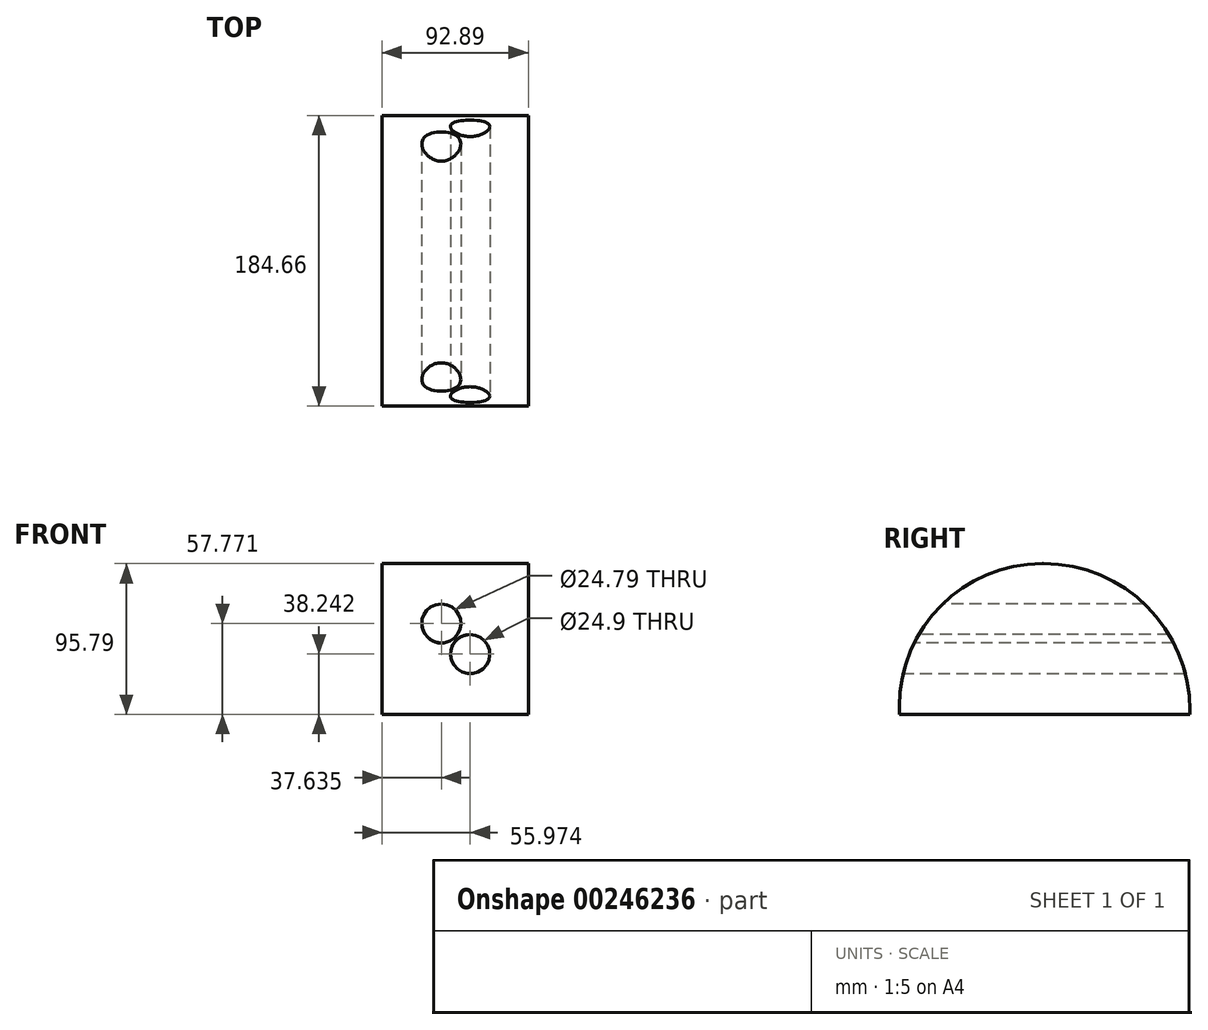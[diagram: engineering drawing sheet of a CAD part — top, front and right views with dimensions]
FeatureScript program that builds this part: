
annotation { "Feature Type Name" : "Feature", "Feature Type Description" : "" }
export const myFeature = defineFeature(function(context is Context, id is Id, definition is map)
    precondition{}
    {
        {
            var Q0;
            Q0=qCreatedBy(makeId("Front.planeOp"),FACE);
            var sketch = newSketch(context, id + "F0", { "sketchPlane" : qUnion([Q0])});
            skLineSegment(sketch, "E0.bottom", {"start": v(-52.5, 35.25) * mm, "end": v(40.39, 35.25) * mm});
            skLineSegment(sketch, "E0.top", {"start": v(-52.5, -60.54) * mm, "end": v(40.39, -60.54) * mm});
            skLineSegment(sketch, "E0.left", {"start": v(-52.5, 35.25) * mm, "end": v(-52.5, -60.54) * mm});
            skLineSegment(sketch, "E0.right", {"start": v(40.39, 35.25) * mm, "end": v(40.39, -60.54) * mm});
            skSolve(sketch);
        }
        {
            var Q0;
            Q0=makeQuery(id+"F0.imprint","IMPRINT",FACE,{"disambiguationData":[TD([[makeQuery(id+"F0.imprint","IMPRINT",EDGE,{"derivedFrom":sQuery(id+"F0.wireOp",EDGE,"E0.bottom")}),-1.0]])]});
            extrude(context, id + "F1", {"entities" : qUnion([Q0]), "depth" : 98.55 * mm});
        }
        {
            var Q0;
            Q0=makeQuery(id+"F1.opExtrude","CAP_FACE",FACE,{"disambiguationData":[OSD([sQuery(id+"F0.wireOp",EDGE,"E0.bottom"),sQuery(id+"F0.wireOp",EDGE,"E0.top"),sQuery(id+"F0.wireOp",EDGE,"E0.left"),sQuery(id+"F0.wireOp",EDGE,"E0.right")])],"isStart":true});
            extrude(context, id + "F2", {"entities" : qUnion([Q0]), "operationType" : NewBodyOperationType.ADD, "depth" : 86.1 * mm});
        }
        {
            var Q0;
            Q0=makeQuery(id+"F1.opExtrude","CAP_FACE",FACE,{"disambiguationData":[OSD([sQuery(id+"F0.wireOp",EDGE,"E0.bottom"),sQuery(id+"F0.wireOp",EDGE,"E0.top"),sQuery(id+"F0.wireOp",EDGE,"E0.left"),sQuery(id+"F0.wireOp",EDGE,"E0.right")])],"isStart":false});
            var sketch = newSketch(context, id + "F3", { "sketchPlane" : qUnion([Q0])});
            skCircle(sketch, "E1", {"center": v(-14.87, -2.77) * mm, "radius": 12.4 * mm});
            skSolve(sketch);
        }
        {
            var Q0;
            Q0 = qSketchRegion(id + "F3", true);
            extrude(context, id + "F4", {"entities" : qUnion([Q0]), "operationType" : NewBodyOperationType.REMOVE, "oppositeDirection" : true, "depth" : 203.2 * mm});
        }
        {
            var Q0;
            Q0=makeQuery(id+"F1.opExtrude","CAP_FACE",FACE,{"disambiguationData":[OSD([sQuery(id+"F0.wireOp",EDGE,"E0.bottom"),sQuery(id+"F0.wireOp",EDGE,"E0.top"),sQuery(id+"F0.wireOp",EDGE,"E0.left"),sQuery(id+"F0.wireOp",EDGE,"E0.right")])],"isStart":false});
            var sketch = newSketch(context, id + "F5", { "sketchPlane" : qUnion([Q0])});
            skCircle(sketch, "E2", {"center": v(3.47, -22.3) * mm, "radius": 12.45 * mm});
            skSolve(sketch);
        }
        {
            var Q0;
            Q0=makeQuery(id+"F5.imprint","IMPRINT",FACE,{"disambiguationData":[TD([[makeQuery(id+"F5.imprint","IMPRINT",EDGE,{"derivedFrom":sQuery(id+"F5.wireOp",EDGE,"E2")}),1.0]])]});
            extrude(context, id + "F6", {"entities" : qUnion([Q0]), "operationType" : NewBodyOperationType.REMOVE, "oppositeDirection" : true, "depth" : 203.2 * mm});
        }
        {
            var Q0;
            Q0=makeQuery(id+"F1.opExtrude","CAP_EDGE",EDGE,{"disambiguationData":[OSD([sQuery(id+"F0.wireOp",EDGE,"E0.bottom")])],"isStart":false});
            fillet(context, id + "F7", {"entities" : qUnion([Q0]), "radius" : 90.76 * mm, "tangentPropagation" : true, "allowEdgeOverflow" : false});
        }
        {
            var Q0;
            Q0=makeQuery(id+"F2.opExtrude","CAP_EDGE",EDGE,{"disambiguationData":[OSD([sQuery(id+"F0.wireOp",EDGE,"E0.bottom")])],"isStart":false});
            fillet(context, id + "F8", {"entities" : qUnion([Q0]), "radius" : 93.2 * mm, "tangentPropagation" : true, "allowEdgeOverflow" : false});
        }
    });
